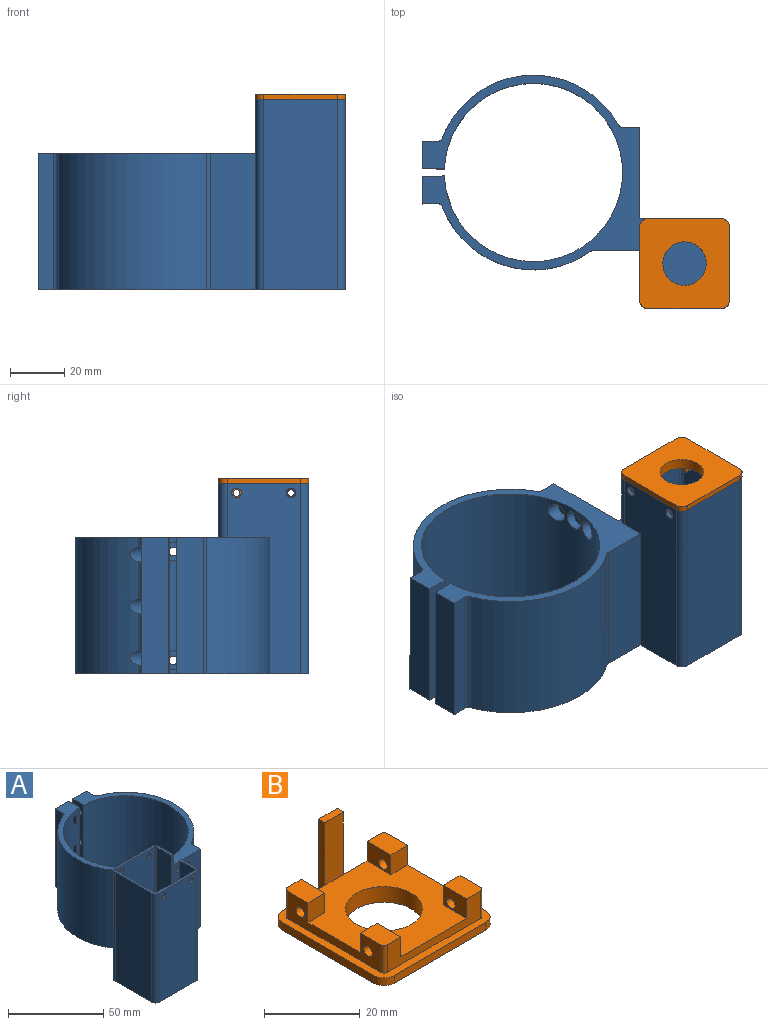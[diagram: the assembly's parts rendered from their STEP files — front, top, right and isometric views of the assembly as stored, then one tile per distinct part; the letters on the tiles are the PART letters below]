
ASSEMBLY  parts=2 mates=1
PART A: 97 faces, bbox 85.8x112.8x70 mm
  f0: plane 33x33mm, normal (0,0,1), area 173.1mm2, adj f14,f15,f16,f17,f78,f79,f80,f81
  f1: plane 82.75x71.5mm, normal (0,0,1), area 1044.1mm2, adj f2,f3,f4,f5,f6,f7,f8,f9
  f2: plane 50x33.5mm, normal (0,-1,0), area 1626.7mm2, adj f1,f3,f17,f18,f19,f20,f21,f22
  f3: plane 50x6.09mm, normal (1,0,0), area 304.7mm2, adj f1,f2,f18,f73
  f4: cylinder r=35.75mm len=64.6mm, axis (0,0,-1), area 4016.7mm2, adj f1,f18,f37,f39,f41,f70,f71,f72
  f5: plane 50x5.38mm, normal (1,-0.03,0), area 203.4mm2, adj f1,f6,f18,f37,f39,f41,f70,f71
  f6: plane 50x10mm, normal (0,1,0), area 500mm2, adj f1,f5,f7,f18
  f7: plane 50x8.02mm, normal (-1,0.03,0), area 372.5mm2, adj f1,f6,f8,f18,f43,f44,f45
  f8: cylinder r=32.75mm len=65.5mm, axis (0,0,-1), area 9879mm2, adj f1,f7,f9,f18,f26,f28,f30,f32
  f9: plane 50x8.02mm, normal (1,0.03,0), area 372.5mm2, adj f1,f8,f10,f18,f46,f47,f48
  f10: plane 50x10mm, normal (0,1,0), area 500mm2, adj f1,f9,f11,f18
  f11: plane 50x5.38mm, normal (-1,-0.03,0), area 269.1mm2, adj f1,f10,f18,f75
  f12: cylinder r=35.75mm len=54.51mm, axis (0,0,-1), area 3288.3mm2, adj f1,f18,f75,f76
  f13: plane 50x16.76mm, normal (-1,0,0), area 837.8mm2, adj f1,f14,f18,f76
  f14: plane 70x27mm, normal (0,1,0), area 1445.8mm2, adj f0,f1,f13,f18,f82,f83,f92,f93
  f15: plane 70x27mm, normal (-1,0,0), area 1890mm2, adj f0,f18,f83,f84
  f16: plane 70x27mm, normal (0,-1,0), area 1870.8mm2, adj f0,f18,f84,f85,f90,f91
  f17: plane 70x30mm, normal (1,0,0), area 1920mm2, adj f0,f1,f2,f18,f82,f85,f94,f95
  f18: plane 112.75x85.75mm, normal (0,0,-1), area 2125.4mm2, adj f2,f3,f4,f5,f6,f7,f8,f9
  f19: cylinder r=1.6mm len=3.2mm, axis (0,-1,0), area 30.2mm2, adj f2,f35
  f20: cylinder r=1.6mm len=3.2mm, axis (0,-1,0), area 30.2mm2, adj f2,f33
  f21: cylinder r=1.6mm len=3.2mm, axis (0,-1,0), area 30.2mm2, adj f2,f31
  f22: cylinder r=1.6mm len=3.2mm, axis (0,-1,0), area 30.2mm2, adj f2,f29
  f23: cylinder r=1.6mm len=3.2mm, axis (0,-1,0), area 30.2mm2, adj f2,f27
  f24: cylinder r=1.6mm len=3.2mm, axis (0,-1,0), area 30.2mm2, adj f2,f25
  f25: plane 7x7mm, normal (0,1,0), area 30.4mm2, adj f24,f26
  f26: cylinder r=3.5mm len=7mm, axis (0,-1,0), area 73.5mm2, adj f8,f25
  f27: plane 7x7mm, normal (0,1,0), area 30.4mm2, adj f23,f28
  f28: cylinder r=3.5mm len=7mm, axis (0,-1,0), area 94.2mm2, adj f8,f27
  f29: plane 7x7mm, normal (0,1,0), area 30.4mm2, adj f22,f30
  f30: cylinder r=3.5mm len=7mm, axis (0,-1,0), area 97mm2, adj f8,f29
  f31: plane 7x7mm, normal (0,1,0), area 30.4mm2, adj f21,f32
  f32: cylinder r=3.5mm len=7mm, axis (0,-1,0), area 73.5mm2, adj f8,f31
  f33: plane 7x7mm, normal (0,1,0), area 30.4mm2, adj f20,f34
  f34: cylinder r=3.5mm len=7mm, axis (0,-1,0), area 94.2mm2, adj f8,f33
  f35: plane 7x7mm, normal (0,1,0), area 30.4mm2, adj f19,f36
  f36: cylinder r=3.5mm len=7mm, axis (0,-1,0), area 97mm2, adj f8,f35
  f37: cylinder r=3.5mm len=8.63mm, axis (1,-0.03,0), area 110.4mm2, adj f4,f5,f38,f70,f71
  f38: plane 7x7mm, normal (1,-0.03,0), area 28.9mm2, adj f37,f45
  f39: cylinder r=3.5mm len=8.63mm, axis (1,-0.03,0), area 110.4mm2, adj f4,f5,f40,f71,f72
  f40: plane 7x7mm, normal (1,-0.03,0), area 28.9mm2, adj f39,f44
  f41: cylinder r=3.5mm len=8.63mm, axis (1,-0.03,0), area 110.4mm2, adj f4,f5,f42,f72,f74
  f42: plane 7x7mm, normal (1,-0.03,0), area 28.9mm2, adj f41,f43
  f43: cylinder r=1.75mm len=6.09mm, axis (1,-0.03,0), area 65.9mm2, adj f7,f42
  f44: cylinder r=1.75mm len=6.09mm, axis (1,-0.03,0), area 65.9mm2, adj f7,f40
  f45: cylinder r=1.75mm len=6.09mm, axis (1,-0.03,0), area 65.9mm2, adj f7,f38
  f46: cylinder r=1.75mm len=3.59mm, axis (1,-0.03,0), area 34.5mm2, adj f9,f59
  f47: cylinder r=1.75mm len=3.59mm, axis (1,-0.03,0), area 34.5mm2, adj f9,f54
  f48: cylinder r=1.75mm len=3.59mm, axis (1,-0.03,0), area 34.5mm2, adj f9,f49
  f49: plane 7.31x6mm, normal (-1,0,0), area 34.2mm2, adj f8,f48,f51,f52,f53
  f50: plane 7.78x6.02mm, normal (1,0,0), area 36.9mm2, adj f8,f51,f52,f53,f65
  f51: plane 7.76x2.5mm, normal (0,0,1), area 18.8mm2, adj f8,f49,f50,f53
  f52: plane 7.76x2.5mm, normal (0,0,-1), area 18.8mm2, adj f8,f49,f50,f53
  f53: plane 6x2.5mm, normal (0,-1,0), area 15mm2, adj f49,f50,f51,f52
  f54: plane 7.31x6mm, normal (-1,0,0), area 34.2mm2, adj f8,f47,f56,f57,f58
  f55: plane 7.78x6.02mm, normal (1,0,0), area 36.9mm2, adj f8,f56,f57,f58,f67
  f56: plane 7.76x2.5mm, normal (0,0,1), area 18.8mm2, adj f8,f54,f55,f58
  f57: plane 7.76x2.5mm, normal (0,0,-1), area 18.8mm2, adj f8,f54,f55,f58
  f58: plane 6x2.5mm, normal (0,-1,0), area 15mm2, adj f54,f55,f56,f57
  f59: plane 7.31x6mm, normal (-1,0,0), area 34.2mm2, adj f8,f46,f61,f62,f63
  f60: plane 7.78x6.02mm, normal (1,0,0), area 36.9mm2, adj f8,f61,f62,f63,f69
  f61: plane 7.76x2.5mm, normal (0,0,1), area 18.8mm2, adj f8,f59,f60,f63
  f62: plane 7.76x2.5mm, normal (0,0,-1), area 18.8mm2, adj f8,f59,f60,f63
  f63: plane 6x2.5mm, normal (0,-1,0), area 15mm2, adj f59,f60,f61,f62
  f64: plane 3.5x3.5mm, normal (1,-0.03,0), area 9.6mm2, adj f65
  f65: cylinder r=1.75mm len=3.55mm, axis (1,-0.03,0), area 18mm2, adj f50,f64
  f66: plane 3.5x3.5mm, normal (1,-0.03,0), area 9.6mm2, adj f67
  f67: cylinder r=1.75mm len=3.55mm, axis (1,-0.03,0), area 18mm2, adj f55,f66
  f68: plane 3.5x3.5mm, normal (1,-0.03,0), area 9.6mm2, adj f69
  f69: cylinder r=1.75mm len=3.55mm, axis (1,-0.03,0), area 18mm2, adj f60,f68
  f70: cylinder r=2mm len=3.34mm, axis (0,0,-1), area 7.1mm2, adj f4,f5,f18,f37
  f71: cylinder r=2mm len=13.68mm, axis (0,0,-1), area 31.6mm2, adj f4,f5,f37,f39
  f72: cylinder r=2mm len=13.68mm, axis (0,0,-1), area 31.6mm2, adj f4,f5,f39,f41
  f73: cylinder r=2mm len=50mm, axis (0,0,-1), area 105.9mm2, adj f1,f3,f4,f18
  f74: cylinder r=2mm len=3.34mm, axis (0,0,-1), area 7.1mm2, adj f1,f4,f5,f41
  f75: cylinder r=2mm len=50mm, axis (0,0,-1), area 123.8mm2, adj f1,f11,f12,f18
  f76: cylinder r=2mm len=50mm, axis (0,0,-1), area 63mm2, adj f1,f12,f13,f18
  f77: plane 30x30mm, normal (0,0,1), area 899.1mm2, adj f78,f79,f80,f81,f86,f87,f88,f89
  f78: plane 68x28mm, normal (-1,0,0), area 1784mm2, adj f0,f77,f88,f89,f94,f95,f96
  f79: plane 68x28mm, normal (0,-1,0), area 1884.8mm2, adj f0,f77,f87,f88,f92,f93
  f80: plane 68x28mm, normal (1,0,0), area 1904mm2, adj f0,f77,f86,f87
  f81: plane 68x28mm, normal (0,1,0), area 1884.8mm2, adj f0,f77,f86,f89,f90,f91
  f82: cylinder r=3mm len=20mm, axis (0,0,-1), area 94.2mm2, adj f0,f1,f14,f17
  f83: cylinder r=3mm len=70mm, axis (0,0,1), area 329.9mm2, adj f0,f14,f15,f18
  f84: cylinder r=3mm len=70mm, axis (0,0,-1), area 329.9mm2, adj f0,f15,f16,f18
  f85: cylinder r=3mm len=70mm, axis (0,0,1), area 329.9mm2, adj f0,f16,f17,f18
  f86: cylinder r=1mm len=68mm, axis (0,0,1), area 106.8mm2, adj f0,f77,f80,f81
  f87: cylinder r=1mm len=68mm, axis (0,0,-1), area 106.8mm2, adj f0,f77,f79,f80
  f88: cylinder r=1mm len=68mm, axis (0,0,1), area 106.8mm2, adj f0,f77,f78,f79
  f89: cylinder r=1mm len=68mm, axis (0,0,-1), area 106.8mm2, adj f0,f77,f78,f81
  f90: cylinder r=1.75mm len=3.5mm, axis (0,-1,0), area 16.5mm2, adj f16,f81
  f91: cylinder r=1.75mm len=3.5mm, axis (0,-1,0), area 16.5mm2, adj f16,f81
  f92: cylinder r=1.75mm len=3.5mm, axis (0,-1,0), area 16.5mm2, adj f14,f79
  f93: cylinder r=1.75mm len=3.5mm, axis (0,-1,0), area 16.5mm2, adj f14,f79
  f94: plane 20x1.5mm, normal (0,1,0), area 30mm2, adj f0,f17,f78,f95
  f95: plane 6x1.5mm, normal (0,0,1), area 9mm2, adj f17,f78,f94,f96
  f96: plane 20x1.5mm, normal (0,-1,0), area 30mm2, adj f0,f17,f78,f95
PART B: 41 faces, bbox 33x33x20 mm
  f0: plane 33x33mm, normal (0,0,1), area 207.9mm2, adj f1,f3,f4,f5,f6,f8,f9,f10
  f1: plane 10.95x7mm, normal (0,1,0), area 41.9mm2, adj f0,f2,f12,f14,f32,f38
  f2: plane 29.4x29.4mm, normal (0,0,1), area 523.3mm2, adj f1,f8,f9,f10,f11,f12,f13,f15
  f3: plane 27x2mm, normal (-1,0,0), area 54mm2, adj f0,f7,f33,f36
  f4: plane 27x2mm, normal (0,-1,0), area 54mm2, adj f0,f7,f33,f34
  f5: plane 27x2mm, normal (1,0,0), area 54mm2, adj f0,f7,f34,f35
  f6: plane 27x20mm, normal (0,1,0), area 153mm2, adj f0,f7,f35,f36,f38,f39,f40
  f7: plane 33x33mm, normal (0,0,-1), area 880.2mm2, adj f3,f4,f5,f6,f24,f33,f34,f35
  f8: plane 27.4x7mm, normal (-1,0,0), area 105mm2, adj f0,f2,f13,f14,f16,f17,f27,f28
  f9: plane 27.4x7mm, normal (0,-1,0), area 94.8mm2, adj f0,f2,f15,f17,f21,f23,f29,f30
  f10: plane 27.4x7mm, normal (1,0,0), area 105mm2, adj f0,f2,f19,f20,f22,f23,f25,f26
  f11: plane 10.95x7mm, normal (0,1,0), area 41.9mm2, adj f0,f2,f18,f20,f31,f39
  f12: plane 7x5mm, normal (1,0,0), area 30.1mm2, adj f1,f2,f13,f14,f28
  f13: plane 5x5mm, normal (0,-1,0), area 25mm2, adj f2,f8,f12,f14
  f14: plane 7x5mm, normal (0,0,1), area 34.8mm2, adj f1,f8,f12,f13,f32
  f15: plane 7x5mm, normal (1,0,0), area 30.1mm2, adj f2,f9,f16,f17,f27
  f16: plane 5x5mm, normal (0,1,0), area 25mm2, adj f2,f8,f15,f17
  f17: plane 7x5mm, normal (0,0,1), area 34.8mm2, adj f8,f9,f15,f16,f29
  f18: plane 7x5mm, normal (-1,0,0), area 30.1mm2, adj f2,f11,f19,f20,f26
  f19: plane 5x5mm, normal (0,-1,0), area 25mm2, adj f2,f10,f18,f20
  f20: plane 7x5mm, normal (0,0,1), area 34.8mm2, adj f10,f11,f18,f19,f31
  f21: plane 7x5mm, normal (-1,0,0), area 30.1mm2, adj f2,f9,f22,f23,f25
  f22: plane 5x5mm, normal (0,1,0), area 25mm2, adj f2,f10,f21,f23
  f23: plane 7x5mm, normal (0,0,1), area 34.8mm2, adj f9,f10,f21,f22,f30
  f24: cylinder r=8mm len=16mm, axis (0,0,-1), area 201.1mm2, adj f2,f7
  f25: cylinder r=1.25mm len=5mm, axis (1,0,0), area 39.3mm2, adj f10,f21
  f26: cylinder r=1.25mm len=5mm, axis (1,0,0), area 39.3mm2, adj f10,f18
  f27: cylinder r=1.25mm len=5mm, axis (1,0,0), area 39.3mm2, adj f8,f15
  f28: cylinder r=1.25mm len=5mm, axis (1,0,0), area 39.3mm2, adj f8,f12
  f29: cylinder r=1mm len=7mm, axis (0,0,-1), area 11mm2, adj f0,f8,f9,f17
  f30: cylinder r=1mm len=7mm, axis (0,0,1), area 11mm2, adj f0,f9,f10,f23
  f31: cylinder r=1mm len=7mm, axis (0,0,-1), area 11mm2, adj f0,f10,f11,f20
  f32: cylinder r=1mm len=7mm, axis (0,0,1), area 11mm2, adj f0,f1,f8,f14
  f33: cylinder r=3mm len=3mm, axis (0,0,-1), area 9.4mm2, adj f0,f3,f4,f7
  f34: cylinder r=3mm len=3mm, axis (0,0,1), area 9.4mm2, adj f0,f4,f5,f7
  f35: cylinder r=3mm len=3mm, axis (0,0,-1), area 9.4mm2, adj f0,f5,f6,f7
  f36: cylinder r=3mm len=3mm, axis (0,0,1), area 9.4mm2, adj f0,f3,f6,f7
  f37: plane 16x5.5mm, normal (0,-1,0), area 88mm2, adj f2,f38,f39,f40
  f38: plane 18x1.8mm, normal (-1,0,0), area 32.4mm2, adj f0,f1,f6,f37,f40
  f39: plane 18x1.8mm, normal (1,0,0), area 32.4mm2, adj f0,f6,f11,f37,f40
  f40: plane 5.5x1.8mm, normal (0,0,1), area 9.9mm2, adj f6,f37,f38,f39
PLACE A rot(axis=(0,0,1),90deg) t=(-14.27,33.59,-82.9)mm
PLACE B rot(axis=(0,-1,0),180deg) t=(57.73,16.59,-10.9)mm
MATE fastened A.f16 <-> B.f3  axis (1,0,0) through (57.73,0.09,-12.9)mm
